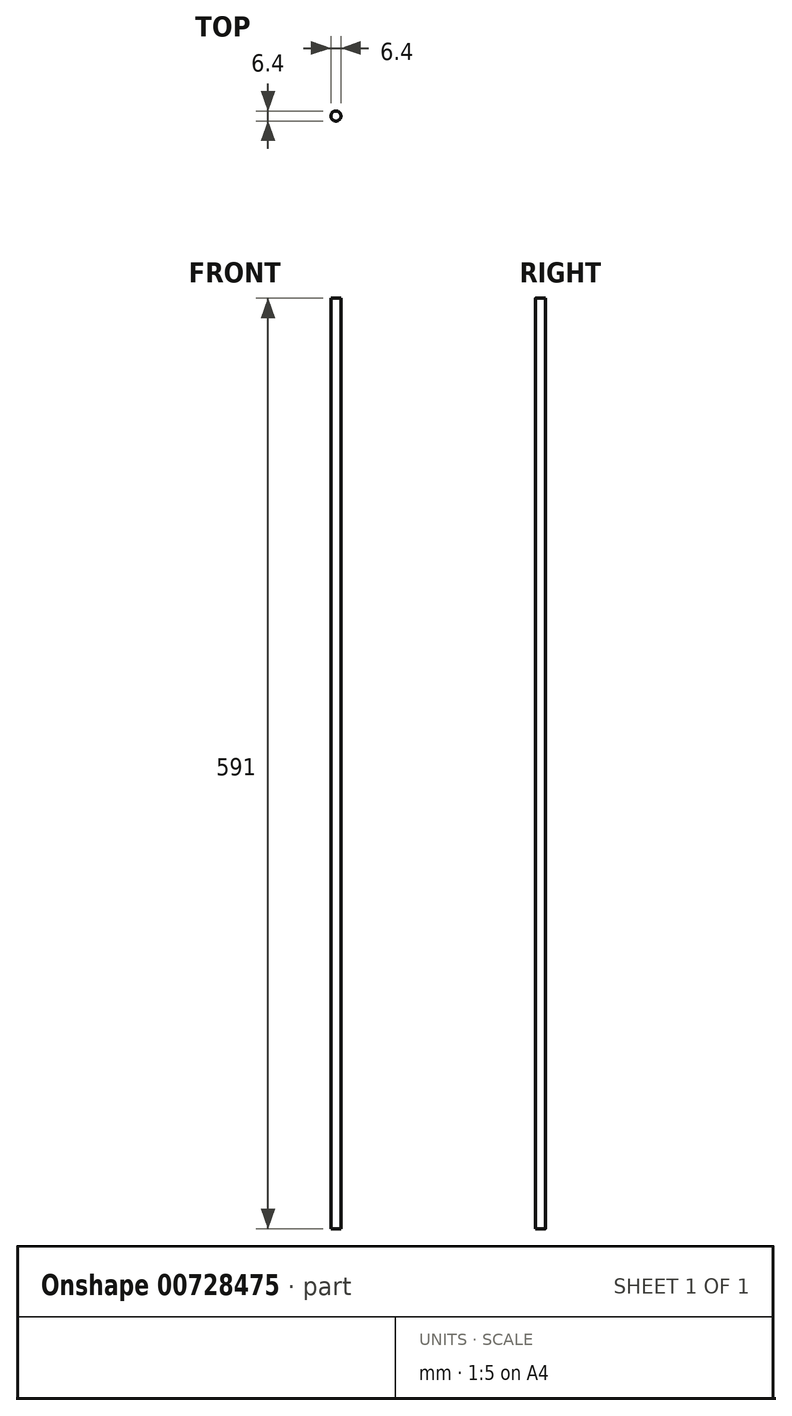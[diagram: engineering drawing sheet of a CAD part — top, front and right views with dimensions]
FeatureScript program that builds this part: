
annotation { "Feature Type Name" : "Feature", "Feature Type Description" : "" }
export const myFeature = defineFeature(function(context is Context, id is Id, definition is map)
    precondition{}
    {
        {
            var Q0;
            Q0=qCreatedBy(makeId("Top.planeOp"),FACE);
            cPlane(context, id + "F0", {"entities" : qUnion([Q0]), "cplaneType" : CPlaneType.OFFSET, "offset" : 1000 * mm, "oppositeDirection" : true, "width" : 150 * mm, "height" : 150 * mm});
        }
        {
            var Q0;
            Q0=qCreatedBy(id+"F0.planeOp",FACE);
            var sketch = newSketch(context, id + "F1", { "sketchPlane" : qUnion([Q0])});
            skCircle(sketch, "E0", {"center": v(0, 0) * mm, "radius": 3.2 * mm});
            skSolve(sketch);
        }
        {
            var Q0;
            Q0=makeQuery(id+"F1.imprint","IMPRINT",FACE,{"disambiguationData":[TD([[makeQuery(id+"F1.imprint","IMPRINT",EDGE,{"derivedFrom":sQuery(id+"F1.wireOp",EDGE,"E0")}),1.0]])]});
            extrude(context, id + "F2", {"entities" : qUnion([Q0]), "depth" : 591 * mm, "offsetDistance" : 25 * mm});
        }
    });
